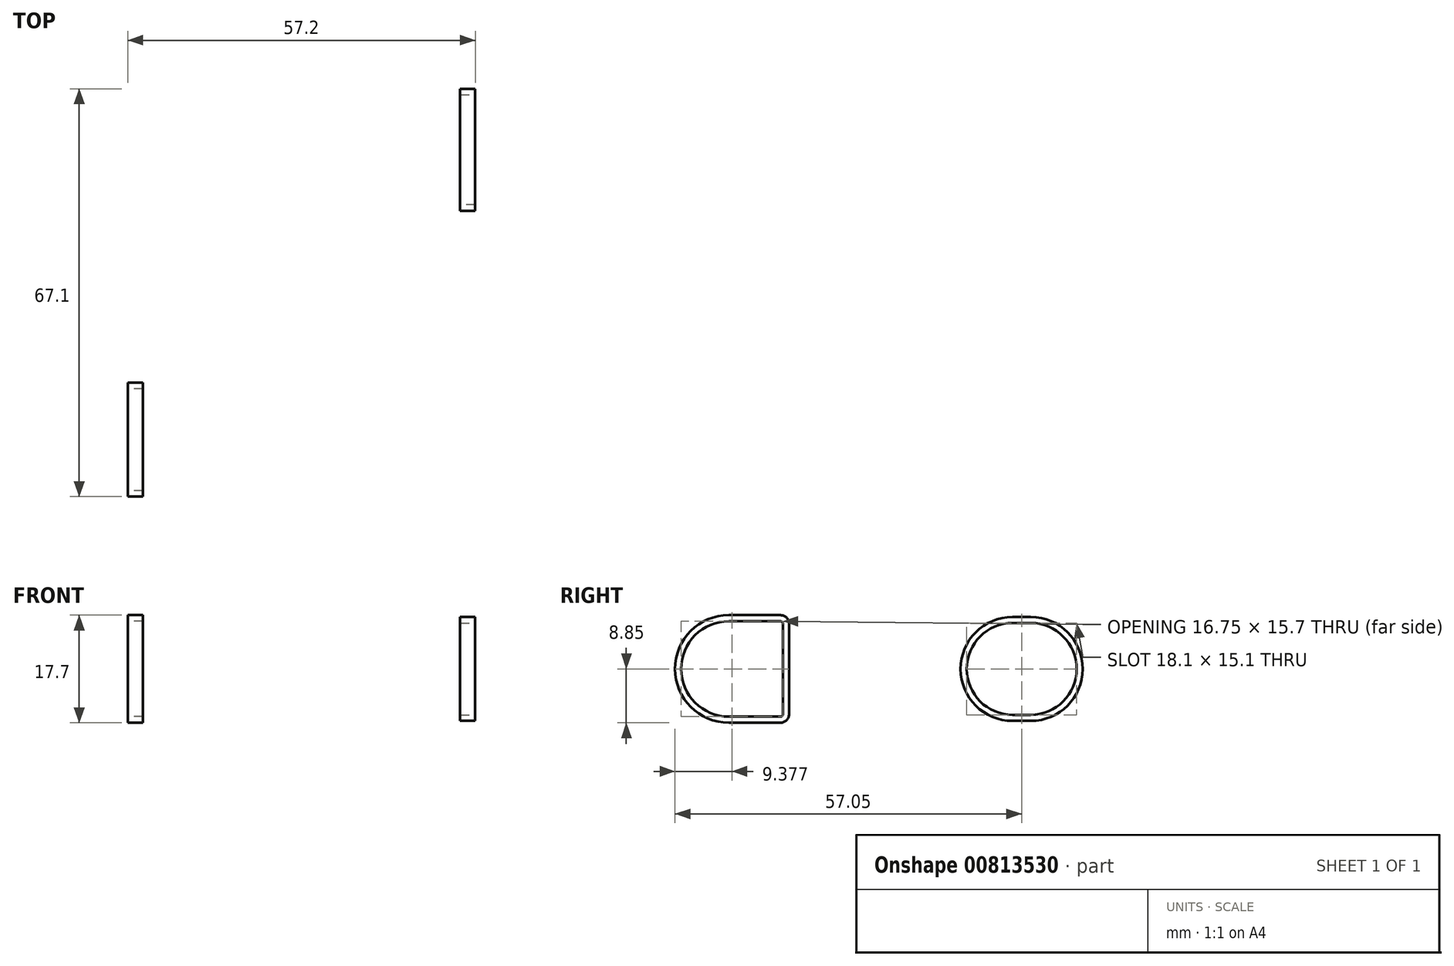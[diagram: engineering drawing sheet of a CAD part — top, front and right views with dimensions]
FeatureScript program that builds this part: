
annotation { "Feature Type Name" : "Feature", "Feature Type Description" : "" }
export const myFeature = defineFeature(function(context is Context, id is Id, definition is map)
    precondition{}
    {
        {
            var Q0;
            Q0=qCreatedBy(makeId("Front.planeOp"),FACE);
            var sketch = newSketch(context, id + "F0", { "sketchPlane" : qUnion([Q0])});
            skLineSegment(sketch, "E0", {"start": v(-11.53, 0) * mm, "end": v(14.53, 0) * mm});
            skLineSegment(sketch, "E1.bottom", {"start": v(-0.9, 8.55) * mm, "end": v(1.6, 8.55) * mm});
            skLineSegment(sketch, "E1.top", {"start": v(-0.9, 7.55) * mm, "end": v(1.6, 7.55) * mm});
            skLineSegment(sketch, "E1.left", {"start": v(-0.9, 8.55) * mm, "end": v(-0.9, 7.55) * mm});
            skLineSegment(sketch, "E1.right", {"start": v(1.6, 8.55) * mm, "end": v(1.6, 7.55) * mm});
            skSolve(sketch);
        }
        {
            var Q0;
            Q0=makeQuery(id+"F0.imprint","IMPRINT",FACE,{"disambiguationData":[TD([[makeQuery(id+"F0.imprint","IMPRINT",EDGE,{"derivedFrom":sQuery(id+"F0.wireOp",EDGE,"E1.bottom")}),-1.0]])]});
            extrude(context, id + "F1", {"entities" : qUnion([Q0]), "oppositeDirection" : true, "depth" : 3 * mm, "offsetDistance" : 25 * mm});
        }
        {
            var Q0;
            Q0=qCreatedBy(makeId("Right.planeOp"),FACE);
            var sketch = newSketch(context, id + "F2", { "sketchPlane" : qUnion([Q0])});
            skCircle(sketch, "E2", {"center": v(0, 0) * mm, "radius": 0.6 * mm});
            skSolve(sketch);
        }
        {
            var Q0;
            Q0=qSketchRegion(id+"F2",true);
            extrude(context, id + "F3", {"entities" : qUnion([Q0]), "depth" : 25 * mm, "offsetDistance" : 25 * mm});
        }
        {
            var Q0;
            Q0=makeQuery(id+"F0.imprint","IMPRINT",FACE,{"disambiguationData":[TD([[makeQuery(id+"F0.imprint","IMPRINT",EDGE,{"derivedFrom":sQuery(id+"F0.wireOp",EDGE,"E1.bottom")}),-1.0]])]});
            var Q1;
            Q1=sQuery(id+"F0.wireOp",EDGE,"E0");
            revolve(context, id + "F4", {"operationType" : NewBodyOperationType.ADD, "surfaceOperationType" : NewSurfaceOperationType.NEW, "entities" : qUnion([Q0]), "axis" : qUnion([Q1]), "revolveType" : RevolveType.ONE_DIRECTION, "angle" : 180 * degree});
        }
        {
            var Q0;
            Q0=makeQuery(id+"F4.opRevolve","CAP_FACE",FACE,{"disambiguationData":[OSD([sQuery(id+"F0.wireOp",EDGE,"E1.bottom"),sQuery(id+"F0.wireOp",EDGE,"E1.top"),sQuery(id+"F0.wireOp",EDGE,"E1.left"),sQuery(id+"F0.wireOp",EDGE,"E1.right")])],"isStart":false});
            extrude(context, id + "F5", {"entities" : qUnion([Q0]), "operationType" : NewBodyOperationType.ADD, "depth" : 3 * mm, "offsetDistance" : 25 * mm});
        }
        {
            var Q0;
            Q0=makeQuery(id+"F3.opExtrude","SWEPT_BODY",BODY,{"disambiguationData":[OSD([sQuery(id+"F2.wireOp",EDGE,"E2")])]});
            deleteBodies(context, id + "F6", {"entities" : qUnion([Q0])});
        }
        {
            var Q0;
            Q0=makeQuery(id+"F1.opExtrude","CAP_FACE",FACE,{"disambiguationData":[OSD([sQuery(id+"F0.wireOp",EDGE,"E1.bottom"),sQuery(id+"F0.wireOp",EDGE,"E1.top"),sQuery(id+"F0.wireOp",EDGE,"E1.left"),sQuery(id+"F0.wireOp",EDGE,"E1.right")])],"isStart":false});
            cPlane(context, id + "F7", {"entities" : qUnion([Q0]), "cplaneType" : CPlaneType.OFFSET, "offset" : 0 * mm, "width" : 150 * mm, "height" : 150 * mm});
        }
        {
            var Q0;
            Q0=qCreatedBy(id+"F7.planeOp",FACE);
            var sketch = newSketch(context, id + "F8", { "sketchPlane" : qUnion([Q0])});
            skLineSegment(sketch, "E3", {"start": v(-8.27, 0) * mm, "end": v(9.97, 0) * mm});
            skSolve(sketch);
        }
        {
            var Q0;
            Q0=makeQuery(id+"F1.opExtrude","CAP_FACE",FACE,{"disambiguationData":[OSD([sQuery(id+"F0.wireOp",EDGE,"E1.bottom"),sQuery(id+"F0.wireOp",EDGE,"E1.top"),sQuery(id+"F0.wireOp",EDGE,"E1.left"),sQuery(id+"F0.wireOp",EDGE,"E1.right")])],"isStart":false});
            var Q1;
            Q1=sQuery(id+"F8.wireOp",EDGE,"E3");
            revolve(context, id + "F9", {"operationType" : NewBodyOperationType.ADD, "surfaceOperationType" : NewSurfaceOperationType.NEW, "entities" : qUnion([Q0]), "axis" : qUnion([Q1]), "revolveType" : RevolveType.ONE_DIRECTION, "angle" : 180 * degree});
        }
        {
            var Q0;
            Q0=makeQuery(id+"F1.opExtrude","SWEPT_BODY",BODY,{"disambiguationData":[OSD([sQuery(id+"F0.wireOp",EDGE,"E1.bottom"),sQuery(id+"F0.wireOp",EDGE,"E1.top"),sQuery(id+"F0.wireOp",EDGE,"E1.left"),sQuery(id+"F0.wireOp",EDGE,"E1.right")])]});
            transform(context, id + "F10", {"entities" : qUnion([Q0]), "transformType" : TransformType.TRANSLATION_3D, "dx" : 55.6 * mm, "dy" : 0 * mm, "dz" : 0 * mm, "makeCopy" : false});
        }
        {
            var Q0;
            Q0=makeQuery(id+"F1.opExtrude","SWEPT_BODY",BODY,{"disambiguationData":[OSD([sQuery(id+"F0.wireOp",EDGE,"E1.bottom"),sQuery(id+"F0.wireOp",EDGE,"E1.top"),sQuery(id+"F0.wireOp",EDGE,"E1.left"),sQuery(id+"F0.wireOp",EDGE,"E1.right")])]});
            transform(context, id + "F11", {"entities" : qUnion([Q0]), "transformType" : TransformType.TRANSLATION_3D, "dx" : 0 * mm, "dy" : 46.7 * mm, "dz" : 0 * mm, "makeCopy" : false});
        }
        {
            var Q0;
            Q0=qCreatedBy(makeId("Right.planeOp"),FACE);
            var sketch = newSketch(context, id + "F12", { "sketchPlane" : qUnion([Q0])});
            skCircle(sketch, "E4", {"center": v(0, 0) * mm, "radius": 7.5 * mm, "construction": true});
            skLineSegment(sketch, "E5.bottom", {"start": v(5.8, 7.75) * mm, "end": v(8.8, 7.75) * mm, "construction": true});
            skLineSegment(sketch, "E5.top", {"start": v(5.8, 4.75) * mm, "end": v(8.8, 4.75) * mm, "construction": true});
            skLineSegment(sketch, "E5.left", {"start": v(5.8, 7.75) * mm, "end": v(5.8, 4.75) * mm, "construction": true});
            skLineSegment(sketch, "E5.right", {"start": v(8.8, 7.75) * mm, "end": v(8.8, 4.75) * mm, "construction": true});
            skLineSegment(sketch, "E6", {"start": v(0, 0) * mm, "end": v(21.58, 0) * mm, "construction": true});
            skLineSegment(sketch, "E7.MirrorCS", {"start": v(5.8, -4.75) * mm, "end": v(8.8, -4.75) * mm, "construction": true});
            skLineSegment(sketch, "E8.MirrorCS", {"start": v(5.8, -7.75) * mm, "end": v(5.8, -4.75) * mm, "construction": true});
            skLineSegment(sketch, "E9.MirrorCS", {"start": v(5.8, -7.75) * mm, "end": v(8.8, -7.75) * mm, "construction": true});
            skLineSegment(sketch, "E10.MirrorCS", {"start": v(8.8, -7.75) * mm, "end": v(8.8, -4.75) * mm, "construction": true});
            skLineSegment(sketch, "E11", {"start": v(0, 7.85) * mm, "end": v(8.5, 7.85) * mm});
            skLineSegment(sketch, "E12", {"start": v(8.9, 7.45) * mm, "end": v(8.9, 0) * mm});
            skArc(sketch, "E13", {"start": v(0, 7.85) * mm, "mid": v(-5.55, 5.55) * mm, "end": v(-7.85, 0) * mm});
            skPoint(sketch, "E14.visualSharp", {"position": v(8.9, 7.85) * mm});
            skArc(sketch, "E14.filletArc", {"start": v(8.9, 7.45) * mm, "mid": v(8.79, 7.73) * mm, "end": v(8.5, 7.85) * mm});
            skArc(sketch, "E15.0", {"start": v(0, 8.85) * mm, "mid": v(-6.26, 6.26) * mm, "end": v(-8.85, 0) * mm});
            skLineSegment(sketch, "E15.1", {"start": v(0, 8.85) * mm, "end": v(8.5, 8.85) * mm});
            skArc(sketch, "E15.2", {"start": v(9.9, 7.45) * mm, "mid": v(9.5, 8.44) * mm, "end": v(8.5, 8.85) * mm});
            skLineSegment(sketch, "E15.3", {"start": v(9.9, 7.45) * mm, "end": v(9.9, 0) * mm});
            skArc(sketch, "E16.MirrorCS", {"start": v(8.9, -7.45) * mm, "mid": v(8.79, -7.73) * mm, "end": v(8.5, -7.85) * mm});
            skLineSegment(sketch, "E17.MirrorCS", {"start": v(8.9, -7.45) * mm, "end": v(8.9, 0) * mm});
            skLineSegment(sketch, "E18.MirrorCS", {"start": v(9.9, -7.45) * mm, "end": v(9.9, 0) * mm});
            skArc(sketch, "E19.MirrorCS", {"start": v(9.9, -7.45) * mm, "mid": v(9.5, -8.44) * mm, "end": v(8.5, -8.85) * mm});
            skLineSegment(sketch, "E20.MirrorCS", {"start": v(0, -7.85) * mm, "end": v(8.5, -7.85) * mm});
            skLineSegment(sketch, "E21.MirrorCS", {"start": v(0, -8.85) * mm, "end": v(8.5, -8.85) * mm});
            skArc(sketch, "E22.MirrorCS", {"start": v(0, -8.85) * mm, "mid": v(-6.26, -6.26) * mm, "end": v(-8.85, 0) * mm});
            skArc(sketch, "E23.MirrorCS", {"start": v(0, -7.85) * mm, "mid": v(-5.55, -5.55) * mm, "end": v(-7.85, 0) * mm});
            skSolve(sketch);
        }
        {
            var Q0;
            Q0=makeQuery(id+"F12.imprint","IMPRINT",FACE,{"disambiguationData":[TD([[makeQuery(id+"F12.imprint","IMPRINT",EDGE,{"derivedFrom":sQuery(id+"F12.wireOp",EDGE,"E11")}),1.0]])]});
            extrude(context, id + "F13", {"entities" : qUnion([Q0]), "depth" : 2.5 * mm, "offsetDistance" : 25 * mm});
        }
    });
